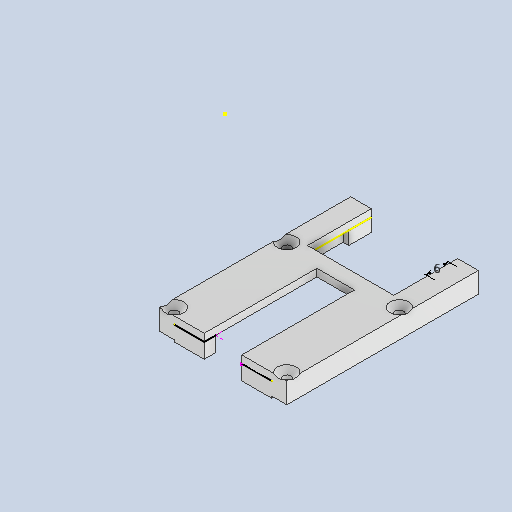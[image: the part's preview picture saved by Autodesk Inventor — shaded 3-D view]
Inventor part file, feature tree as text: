
AUTODESK INVENTOR PART (.ipt)
format: ipt  version: 2025 (Build 290162010, 162A)  size: 244,736 bytes
history: native  units: mm
features: extrude x4, sketch x4, hole x1
ambient origin geometry x8: Origin, YZ Plane, XZ Plane, XY Plane, X Axis, Y Axis, Z Axis, Center Point
bodies: Volumenkörper1 (feature_tree)
feature tree (9):
  extrude  "Extrusion1"  Depth=51.0mm
  extrude  "Extrusion2"  Depth=4.0mm
  hole  "Bohrung1"  [1 undecoded]
  sketch  "Skizze6"  dims[d8=2.2mm d9=6.0mm d10=5.0mm d11=2.0mm d12=90.0deg d13=8.0mm d14=20.594885mm d24=2.0mm d37=19.0mm d38=23.0mm d39=17.0mm d44=4.0mm d47=26.0mm d48=6.0mm d49=2.0mm d50=0.0mm d52=4.0mm d53=0.0mm d54=10.0mm d25=0.5mm d26=0.872665mm d27=0.5mm d28=0.872665mm]
  extrude  "Extrusion5"  Depth=0.5mm
  extrude  "Extrusion6"  Depth=0.5mm
  sketch  "Skizze1"  dims[d0=4.0mm d1=51.0mm]
  sketch  "Skizze2"  dims[d2=26.0mm d3=4.0mm]
  sketch  "Skizze3"  dims[d4=3.5mm d5=0.0mm d6=2.0mm d7=0.0mm]
note: 1 required parameter value undecoded (feature->parameter linkage not recoverable at this tier; creation-order binding heuristic only, values carry confidence <= 0.55)
